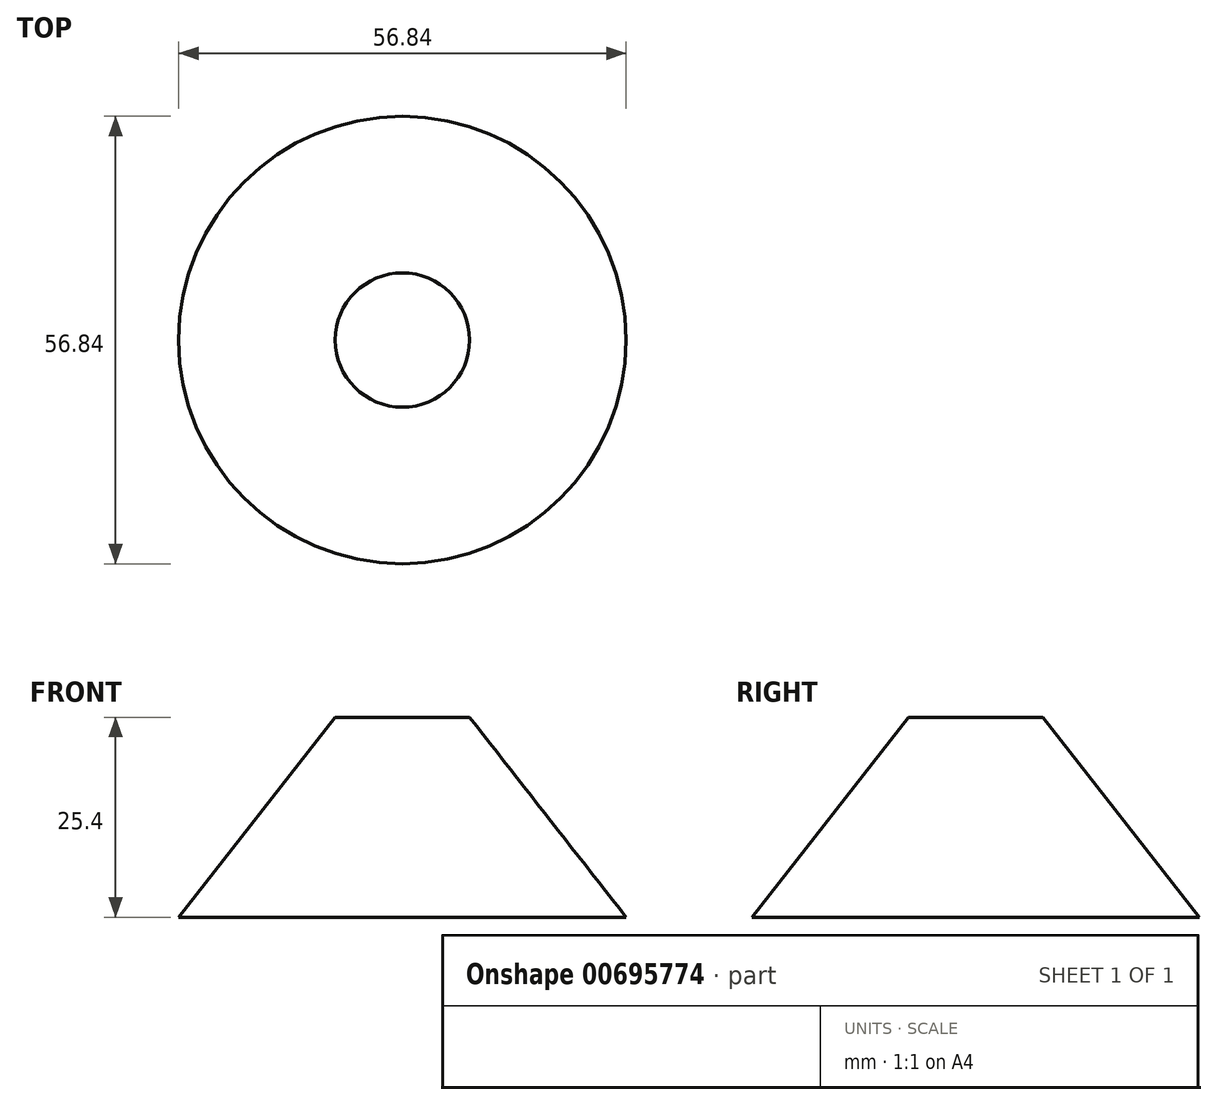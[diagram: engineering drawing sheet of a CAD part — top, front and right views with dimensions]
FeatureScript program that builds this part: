
annotation { "Feature Type Name" : "Feature", "Feature Type Description" : "" }
export const myFeature = defineFeature(function(context is Context, id is Id, definition is map)
    precondition{}
    {
        {
            var Q0;
            Q0=qCreatedBy(makeId("Top.planeOp"),FACE);
            cPlane(context, id + "F0", {"entities" : qUnion([Q0]), "cplaneType" : CPlaneType.OFFSET, "offset" : 25.4 * mm, "width" : 152.4 * mm, "height" : 152.4 * mm});
        }
        {
            var Q0;
            Q0=qCreatedBy(makeId("Top.planeOp"),FACE);
            var sketch = newSketch(context, id + "F1", { "sketchPlane" : qUnion([Q0])});
            skCircle(sketch, "E0", {"center": v(0, 0) * mm, "radius": 28.42 * mm});
            skSolve(sketch);
        }
        {
            var Q0;
            Q0=qCreatedBy(id+"F0.planeOp",FACE);
            var sketch = newSketch(context, id + "F2", { "sketchPlane" : qUnion([Q0])});
            skCircle(sketch, "E1", {"center": v(0, 0) * mm, "radius": 8.54 * mm});
            skSolve(sketch);
        }
        {
            var Q0;
            Q0=makeQuery(id+"F1.imprint","IMPRINT",FACE,{"disambiguationData":[TD([[makeQuery(id+"F1.imprint","IMPRINT",EDGE,{"derivedFrom":sQuery(id+"F1.wireOp",EDGE,"E0")}),1.0]])]});
            var Q1;
            Q1=makeQuery(id+"F2.imprint","IMPRINT",FACE,{"disambiguationData":[TD([[makeQuery(id+"F2.imprint","IMPRINT",EDGE,{"derivedFrom":sQuery(id+"F2.wireOp",EDGE,"E1")}),1.0]])]});
            loft(context, id + "F3", {"sheetProfilesArray" : [{ "sheetProfileEntities" : qUnion([Q0]) }, { "sheetProfileEntities" : qUnion([Q1]) }]});
        }
    });
